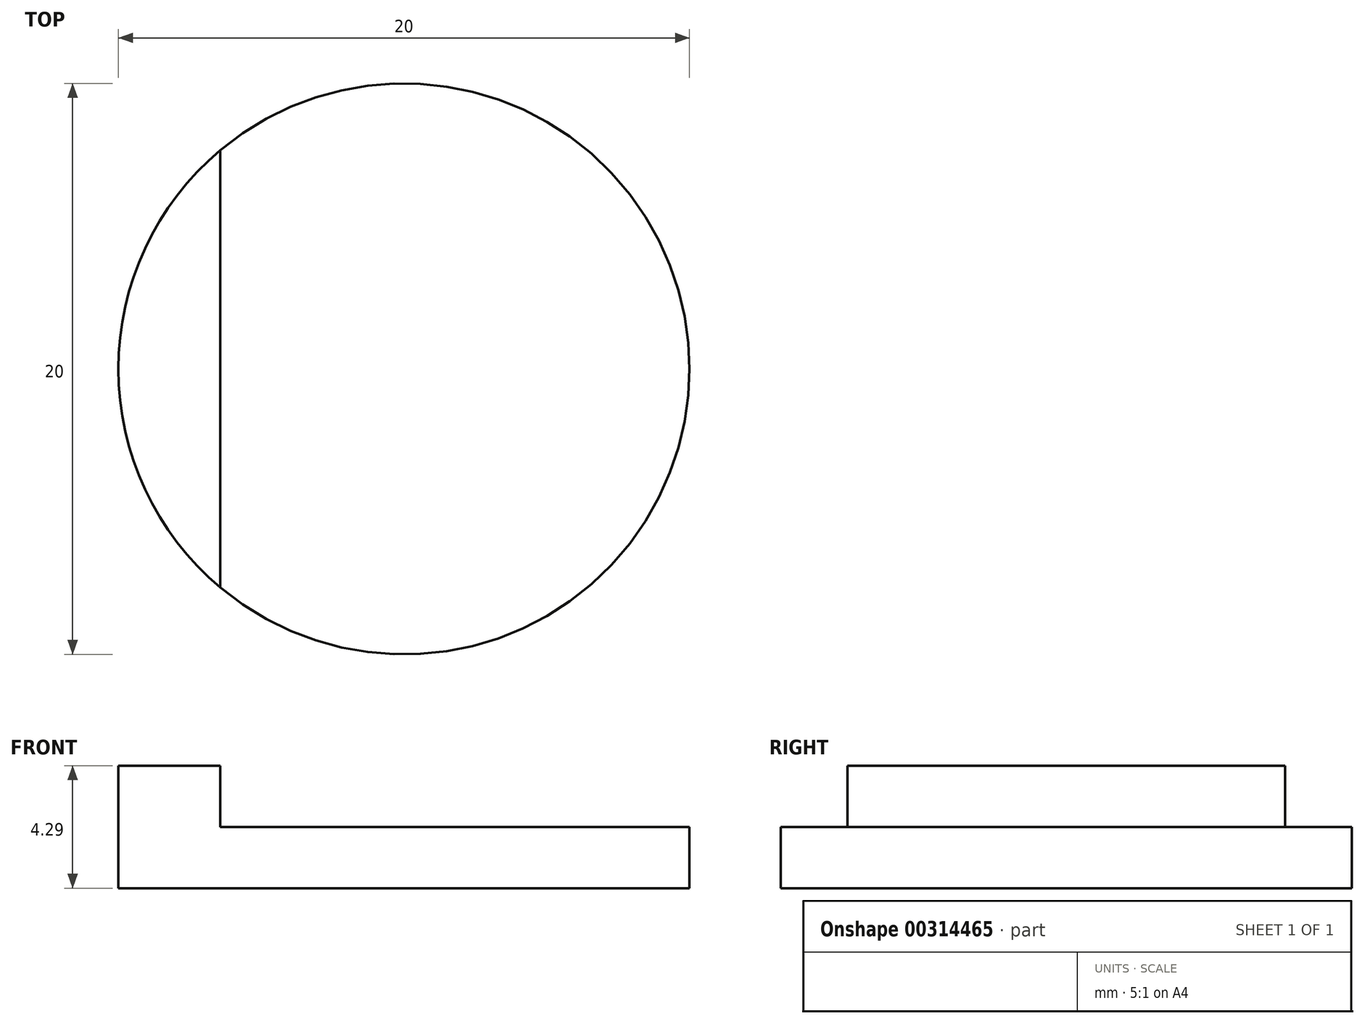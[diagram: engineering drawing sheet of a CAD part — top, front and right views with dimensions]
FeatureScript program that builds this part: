
annotation { "Feature Type Name" : "Feature", "Feature Type Description" : "" }
export const myFeature = defineFeature(function(context is Context, id is Id, definition is map)
    precondition{}
    {
        {
            var Q0;
            Q0=qCreatedBy(makeId("Top.planeOp"),FACE);
            var sketch = newSketch(context, id + "F0", { "sketchPlane" : qUnion([Q0])});
            skCircle(sketch, "E0", {"center": v(0, 0) * mm, "radius": 14 * mm});
            skSolve(sketch);
        }
        {
            var Q0;
            Q0=makeQuery(id+"F0.imprint","IMPRINT",FACE,{"disambiguationData":[TD([[makeQuery(id+"F0.imprint","IMPRINT",EDGE,{"derivedFrom":sQuery(id+"F0.wireOp",EDGE,"E0")}),1.0]])]});
            extrude(context, id + "F1", {"entities" : qUnion([Q0]), "depth" : 3 * mm});
        }
        {
            var Q0;
            Q0=makeQuery(id+"F1.opExtrude","CAP_FACE",FACE,{"disambiguationData":[OSD([sQuery(id+"F0.wireOp",EDGE,"E0")])],"isStart":false});
            var sketch = newSketch(context, id + "F2", { "sketchPlane" : qUnion([Q0])});
            skLineSegment(sketch, "E1.bottom", {"start": v(-9, -14) * mm, "end": v(-14, -14) * mm});
            skLineSegment(sketch, "E1.top", {"start": v(-9, 14) * mm, "end": v(-14, 14) * mm});
            skLineSegment(sketch, "E1.left", {"start": v(-9, -14) * mm, "end": v(-9, 14) * mm});
            skLineSegment(sketch, "E1.right", {"start": v(-14, -14) * mm, "end": v(-14, 14) * mm});
            skPoint(sketch, "E1.middle", {"position": v(-11.5, 0) * mm});
            skLineSegment(sketch, "E2.1.0.0", {"start": v(-4, -14) * mm, "end": v(-9, -14) * mm});
            skLineSegment(sketch, "E2.1.0.1", {"start": v(-4, 14) * mm, "end": v(-9, 14) * mm});
            skLineSegment(sketch, "E2.1.0.2", {"start": v(-4, -14) * mm, "end": v(-4, 14) * mm});
            skPoint(sketch, "E2.1.0.4", {"position": v(-6.5, 0) * mm});
            skLineSegment(sketch, "E2.2.0.0", {"start": v(1, -14) * mm, "end": v(-4, -14) * mm});
            skLineSegment(sketch, "E2.2.0.1", {"start": v(1, 14) * mm, "end": v(-4, 14) * mm});
            skLineSegment(sketch, "E2.2.0.2", {"start": v(1, -14) * mm, "end": v(1, 14) * mm});
            skLineSegment(sketch, "E2.2.0.3", {"start": v(-4, -14) * mm, "end": v(-4, 14) * mm});
            skPoint(sketch, "E2.2.0.4", {"position": v(-1.5, 0) * mm});
            skLineSegment(sketch, "E2.direction1", {"start": v(-14, -14) * mm, "end": v(-9, -14) * mm, "construction": true});
            skLineSegment(sketch, "E3.0.3.0", {"start": v(6, -14) * mm, "end": v(1, -14) * mm});
            skLineSegment(sketch, "E3.3.3.0", {"start": v(6, 14) * mm, "end": v(1, 14) * mm});
            skLineSegment(sketch, "E3.6.3.0", {"start": v(6, -14) * mm, "end": v(6, 14) * mm});
            skPoint(sketch, "E3.12.3.0", {"position": v(3.5, 0) * mm});
            skLineSegment(sketch, "E3.0.4.0", {"start": v(11, -14) * mm, "end": v(6, -14) * mm});
            skLineSegment(sketch, "E3.3.4.0", {"start": v(11, 14) * mm, "end": v(6, 14) * mm});
            skLineSegment(sketch, "E3.6.4.0", {"start": v(11, -14) * mm, "end": v(11, 14) * mm});
            skLineSegment(sketch, "E3.9.4.0", {"start": v(6, -14) * mm, "end": v(6, 14) * mm});
            skPoint(sketch, "E3.12.4.0", {"position": v(8.5, 0) * mm});
            skLineSegment(sketch, "E3.0.5.0", {"start": v(16, -14) * mm, "end": v(11, -14) * mm});
            skLineSegment(sketch, "E3.3.5.0", {"start": v(16, 14) * mm, "end": v(11, 14) * mm});
            skLineSegment(sketch, "E3.6.5.0", {"start": v(16, -14) * mm, "end": v(16, 14) * mm});
            skLineSegment(sketch, "E3.9.5.0", {"start": v(11, -14) * mm, "end": v(11, 14) * mm});
            skPoint(sketch, "E3.12.5.0", {"position": v(13.5, 0) * mm});
            skLineSegment(sketch, "E3.0.6.0", {"start": v(21, -14) * mm, "end": v(16, -14) * mm});
            skLineSegment(sketch, "E3.3.6.0", {"start": v(21, 14) * mm, "end": v(16, 14) * mm});
            skLineSegment(sketch, "E3.6.6.0", {"start": v(21, -14) * mm, "end": v(21, 14) * mm});
            skLineSegment(sketch, "E3.9.6.0", {"start": v(16, -14) * mm, "end": v(16, 14) * mm});
            skPoint(sketch, "E3.12.6.0", {"position": v(18.5, 0) * mm});
            skLineSegment(sketch, "E3.0.7.0", {"start": v(26, -14) * mm, "end": v(21, -14) * mm});
            skLineSegment(sketch, "E3.3.7.0", {"start": v(26, 14) * mm, "end": v(21, 14) * mm});
            skLineSegment(sketch, "E3.6.7.0", {"start": v(26, -14) * mm, "end": v(26, 14) * mm});
            skLineSegment(sketch, "E3.9.7.0", {"start": v(21, -14) * mm, "end": v(21, 14) * mm});
            skPoint(sketch, "E3.12.7.0", {"position": v(23.5, 0) * mm});
            skSolve(sketch);
        }
        {
            var Q0;
            {var subQ0=sQuery(id+"F2.wireOp",EDGE,"E3.9.4.0");var subQ1=makeQuery(id+"F1.opExtrude","CAP_EDGE",EDGE,{"disambiguationData":[OSD([sQuery(id+"F0.wireOp",EDGE,"E0")])],"isStart":false});var subQ2=makeQuery(id+"F2.imprint","INTERSECT",VERTEX,{"disambiguationData":[OD(0.0)],"derivedFrom":[subQ1,subQ0]});Q0=makeQuery(id+"F2.imprint","IMPRINT",FACE,{"disambiguationData":[TD([[makeQuery(id+"F2.imprint","IMPRINT",EDGE,{"disambiguationData":[TD([[subQ2,-1.0]])],"derivedFrom":subQ0}),-1.0]])]});}
            var Q1;
            {var subQ0=sQuery(id+"F2.wireOp",EDGE,"E1.left");var subQ1=makeQuery(id+"F1.opExtrude","CAP_EDGE",EDGE,{"disambiguationData":[OSD([sQuery(id+"F0.wireOp",EDGE,"E0")])],"isStart":false});var subQ2=makeQuery(id+"F2.imprint","INTERSECT",VERTEX,{"disambiguationData":[OD(0.0)],"derivedFrom":[subQ1,subQ0]});Q1=makeQuery(id+"F2.imprint","IMPRINT",FACE,{"disambiguationData":[TD([[makeQuery(id+"F2.imprint","IMPRINT",EDGE,{"disambiguationData":[TD([[subQ2,-1.0]])],"derivedFrom":subQ0}),1.0]])]});}
            var Q2;
            {var subQ0=makeQuery(id+"F1.opExtrude","CAP_EDGE",EDGE,{"disambiguationData":[OSD([sQuery(id+"F0.wireOp",EDGE,"E0")])],"isStart":false});var subQ5=sQuery(id+"F2.wireOp",EDGE,"E2.2.0.3");var subQ6=makeQuery(id+"F2.imprint","INTERSECT",VERTEX,{"disambiguationData":[OD(0.0)],"derivedFrom":[subQ0,subQ5]});Q2=makeQuery(id+"F2.imprint","IMPRINT",FACE,{"disambiguationData":[TD([[makeQuery(id+"F2.imprint","IMPRINT",EDGE,{"disambiguationData":[TD([[subQ6,-1.0]])],"derivedFrom":subQ5}),-1.0]])]});}
            extrude(context, id + "F3", {"entities" : qUnion([Q0, Q1, Q2]), "operationType" : NewBodyOperationType.ADD, "depth" : 3 * mm});
        }
        {
            var Q0;
            Q0=makeQuery(id+"F1.opExtrude","SWEPT_BODY",BODY,{"disambiguationData":[OSD([sQuery(id+"F0.wireOp",EDGE,"E0")])]});
            var Q1;
            Q1=qCreatedBy(makeId("Origin.pointOp"),VERTEX);
            var Q2;
            Q2=qCreatedBy(makeId("Origin.pointOp"),VERTEX);
            transform(context, id + "F4", {"entities" : qUnion([Q0]), "transformType" : TransformType.SCALE_UNIFORMLY, "scale" : 0.71, "scalePoint" : qUnion([Q2]), "makeCopy" : false});
        }
    });
